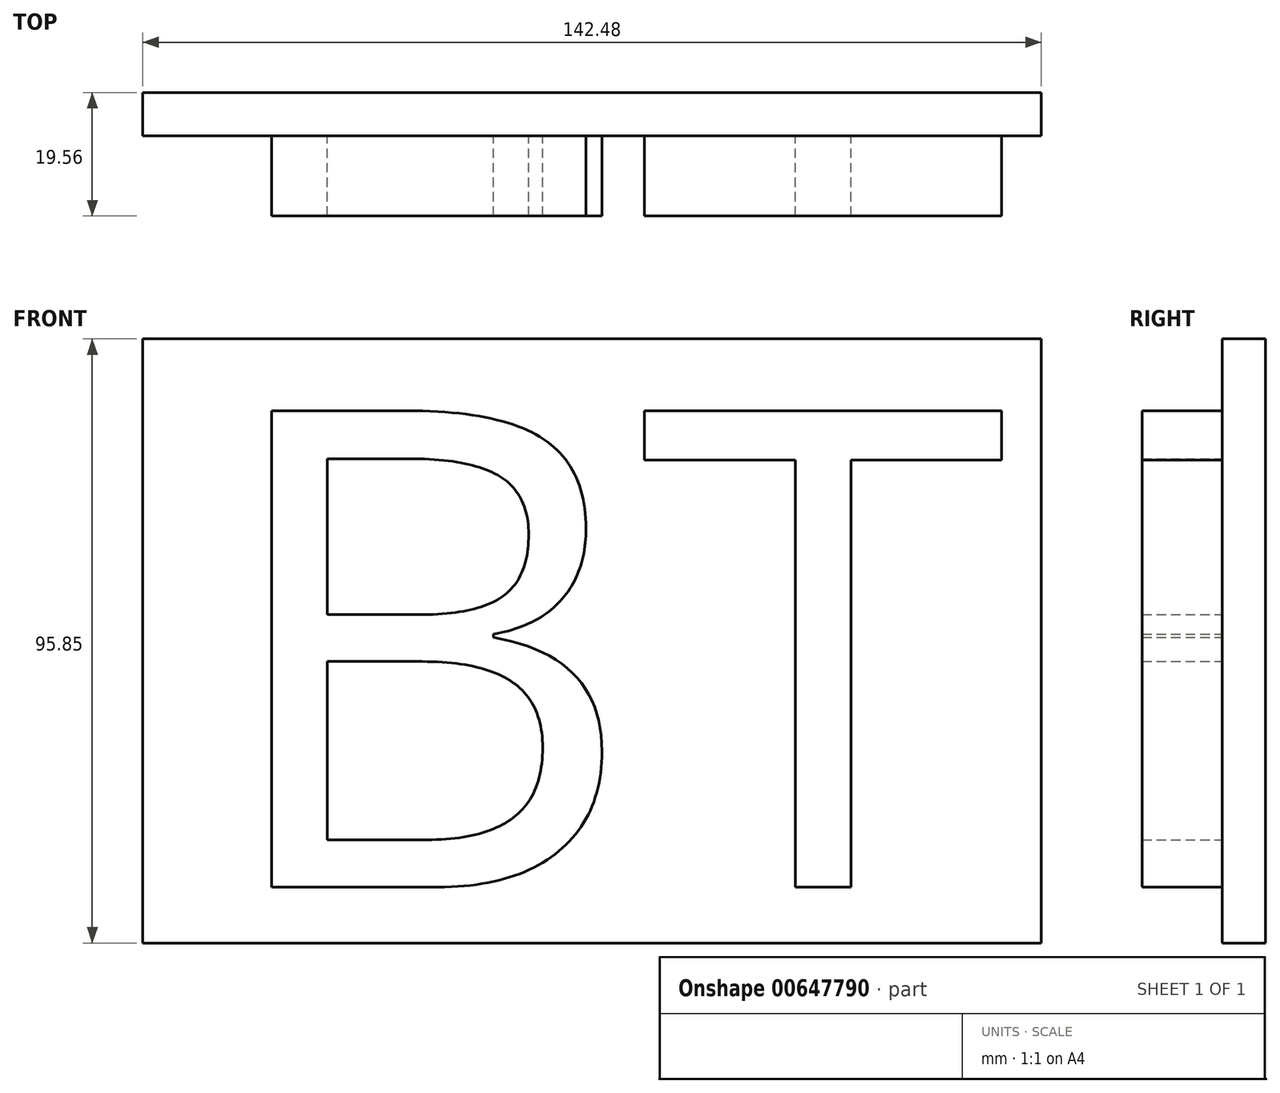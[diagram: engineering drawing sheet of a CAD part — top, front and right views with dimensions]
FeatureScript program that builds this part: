
annotation { "Feature Type Name" : "Feature", "Feature Type Description" : "" }
export const myFeature = defineFeature(function(context is Context, id is Id, definition is map)
    precondition{}
    {
        {
            var Q0;
            Q0=qCreatedBy(makeId("Front.planeOp"),FACE);
            var sketch = newSketch(context, id + "F0", { "sketchPlane" : qUnion([Q0])});
            skText(sketch, "E0", { "text": "BT", "fontName": "OpenSans-Regular.ttf"});
            const initialGuessF0  = {"E0": [-0.06107, -0.03675, 1, 0, 0.0762]};
            skSetInitialGuess(sketch, initialGuessF0);
            skSolve(sketch);
        }
        {
            var Q0;
            Q0=makeQuery(id+"F0.imprint","IMPRINT",FACE,{"disambiguationData":[TD([[makeQuery(id+"F0.imprint","IMPRINT",EDGE,{"derivedFrom":sQuery(id+"F0.wireOp",EDGE,"E0.sketch_text.stroke-0")}),-1.0]])]});
            var Q1;
            Q1=makeQuery(id+"F0.imprint","IMPRINT",FACE,{"disambiguationData":[TD([[makeQuery(id+"F0.imprint","IMPRINT",EDGE,{"derivedFrom":sQuery(id+"F0.wireOp",EDGE,"E0.sketch_text.stroke-25")}),-1.0]])]});
            extrude(context, id + "F1", {"entities" : qUnion([Q0, Q1]), "depth" : 12.7 * mm, "offsetDistance" : 25.4 * mm});
        }
        {
            var Q0;
            Q0=qCreatedBy(makeId("Front.planeOp"),FACE);
            var sketch = newSketch(context, id + "F2", { "sketchPlane" : qUnion([Q0])});
            skLineSegment(sketch, "E1.bottom", {"start": v(-71.14, 50.22) * mm, "end": v(71.34, 50.22) * mm});
            skLineSegment(sketch, "E1.top", {"start": v(-71.14, -45.63) * mm, "end": v(71.34, -45.63) * mm});
            skLineSegment(sketch, "E1.left", {"start": v(-71.14, 50.22) * mm, "end": v(-71.14, -45.63) * mm});
            skLineSegment(sketch, "E1.right", {"start": v(71.34, 50.22) * mm, "end": v(71.34, -45.63) * mm});
            skSolve(sketch);
        }
        {
            var Q0;
            Q0 = qSketchRegion(id + "F2", true);
            extrude(context, id + "F3", {"entities" : qUnion([Q0]), "operationType" : NewBodyOperationType.ADD, "oppositeDirection" : true, "depth" : 6.86 * mm, "offsetDistance" : 25.4 * mm});
        }
    });
